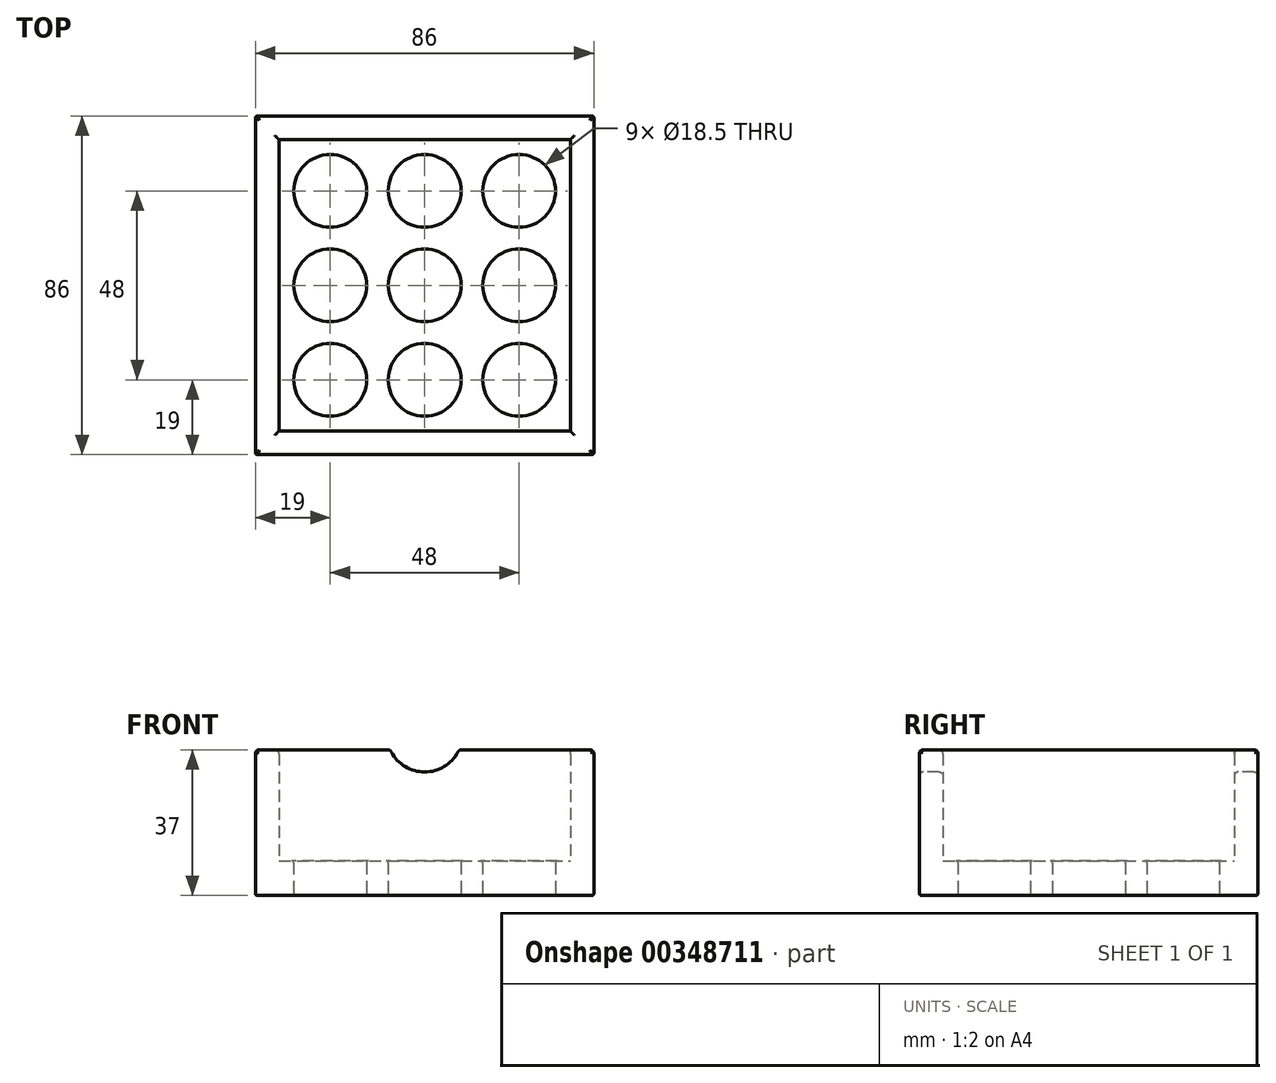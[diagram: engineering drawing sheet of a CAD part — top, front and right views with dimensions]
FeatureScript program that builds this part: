
annotation { "Feature Type Name" : "Feature", "Feature Type Description" : "" }
export const myFeature = defineFeature(function(context is Context, id is Id, definition is map)
    precondition{}
    {
        {
            var Q0;
            Q0=qCreatedBy(makeId("Top.planeOp"),FACE);
            var sketch = newSketch(context, id + "F0", { "sketchPlane" : qUnion([Q0])});
            skLineSegment(sketch, "E0.bottom", {"start": v(0, 0) * mm, "end": v(74, 0) * mm});
            skLineSegment(sketch, "E0.top", {"start": v(0, 74) * mm, "end": v(74, 74) * mm});
            skLineSegment(sketch, "E0.left", {"start": v(0, 0) * mm, "end": v(0, 74) * mm});
            skLineSegment(sketch, "E0.right", {"start": v(74, 0) * mm, "end": v(74, 74) * mm});
            skCircle(sketch, "E1", {"center": v(13, 13) * mm, "radius": 9.25 * mm});
            skCircle(sketch, "E2.0.1.0", {"center": v(13, 37) * mm, "radius": 9.25 * mm});
            skCircle(sketch, "E2.0.2.0", {"center": v(13, 61) * mm, "radius": 9.25 * mm});
            skCircle(sketch, "E2.1.0.0", {"center": v(37, 13) * mm, "radius": 9.25 * mm});
            skCircle(sketch, "E2.1.1.0", {"center": v(37, 37) * mm, "radius": 9.25 * mm});
            skCircle(sketch, "E2.1.2.0", {"center": v(37, 61) * mm, "radius": 9.25 * mm});
            skCircle(sketch, "E2.2.0.0", {"center": v(61, 13) * mm, "radius": 9.25 * mm});
            skCircle(sketch, "E2.2.1.0", {"center": v(61, 37) * mm, "radius": 9.25 * mm});
            skCircle(sketch, "E2.2.2.0", {"center": v(61, 61) * mm, "radius": 9.25 * mm});
            skLineSegment(sketch, "E2.direction1", {"start": v(13, 13) * mm, "end": v(37, 13) * mm, "construction": true});
            skLineSegment(sketch, "E2.direction2", {"start": v(13, 13) * mm, "end": v(13, 37) * mm, "construction": true});
            skLineSegment(sketch, "E3", {"start": v(0, 0) * mm, "end": v(-6, 0) * mm, "construction": true});
            skLineSegment(sketch, "E4", {"start": v(-6, 0) * mm, "end": v(-6, -6) * mm});
            skLineSegment(sketch, "E5.bottom", {"start": v(-6, -6) * mm, "end": v(80, -6) * mm});
            skLineSegment(sketch, "E5.top", {"start": v(-6, 80) * mm, "end": v(80, 80) * mm});
            skLineSegment(sketch, "E5.left", {"start": v(-6, -6) * mm, "end": v(-6, 80) * mm});
            skLineSegment(sketch, "E5.right", {"start": v(80, -6) * mm, "end": v(80, 80) * mm});
            skLineSegment(sketch, "E6", {"start": v(74, 74) * mm, "end": v(80, 74) * mm, "construction": true});
            skLineSegment(sketch, "E7", {"start": v(80, 74) * mm, "end": v(74, 74) * mm, "construction": true});
            skLineSegment(sketch, "E8", {"start": v(74, 74) * mm, "end": v(74, 80) * mm, "construction": true});
            skSolve(sketch);
        }
        {
            var Q0;
            Q0=makeQuery(id+"F0.imprint","IMPRINT",FACE,{"disambiguationData":[TD([[makeQuery(id+"F0.imprint","IMPRINT",EDGE,{"derivedFrom":sQuery(id+"F0.wireOp",EDGE,"E0.bottom")}),-1.0]])]});
            extrude(context, id + "F1", {"entities" : qUnion([Q0]), "depth" : 37 * mm});
        }
        {
            var Q0;
            Q0=makeQuery(id+"F0.imprint","IMPRINT",FACE,{"disambiguationData":[TD([[makeQuery(id+"F0.imprint","IMPRINT",EDGE,{"derivedFrom":sQuery(id+"F0.wireOp",EDGE,"E0.bottom")}),1.0]])]});
            extrude(context, id + "F2", {"entities" : qUnion([Q0]), "operationType" : NewBodyOperationType.ADD, "depth" : 8.8 * mm});
        }
        {
            var Q0;
            Q0=makeQuery(id+"F1.opExtrude","SWEPT_FACE",FACE,{"disambiguationData":[OSD([sQuery(id+"F0.wireOp",EDGE,"E5.bottom")])]});
            var sketch = newSketch(context, id + "F3", { "sketchPlane" : qUnion([Q0])});
            skLineSegment(sketch, "E9", {"start": v(37, 37) * mm, "end": v(37, 41) * mm, "construction": true});
            skPoint(sketch, "E9.endSnap0", {"position": v(37, 37) * mm});
            skCircle(sketch, "E10", {"center": v(37, 41) * mm, "radius": 9.64 * mm});
            skSolve(sketch);
        }
        {
            var Q0;
            Q0 = qSketchRegion(id + "F3", true);
            extrude(context, id + "F4", {"entities" : qUnion([Q0]), "operationType" : NewBodyOperationType.REMOVE, "oppositeDirection" : true, "depth" : 800 * mm});
        }
        {
            var Q0;
            {var subQ0=sQuery(id+"F0.wireOp",EDGE,"E5.bottom");var subQ1=sQuery(id+"F0.wireOp",EDGE,"E0.left");var subQ2=sQuery(id+"F0.wireOp",EDGE,"E0.top");var subQ3=sQuery(id+"F0.wireOp",EDGE,"E0.bottom");var subQ4=sQuery(id+"F0.wireOp",EDGE,"E5.top");var subQ5=sQuery(id+"F0.wireOp",EDGE,"E5.left");Q0=makeQuery(id+"F4.boolean.opBoolean","SPLIT",FACE,{"disambiguationData":[TD([makeQuery(id+"F1.opExtrude","SWEPT_FACE",FACE,{"disambiguationData":[OSD([subQ1])]})])],"derivedFrom":makeQuery(id+"F1.opExtrude","CAP_FACE",FACE,{"disambiguationData":[OSD([subQ3,subQ2,subQ1,sQuery(id+"F0.wireOp",EDGE,"E0.right"),subQ0,subQ4,subQ5,sQuery(id+"F0.wireOp",EDGE,"E5.right")])],"isStart":false})});}
            var Q1;
            {var subQ0=sQuery(id+"F0.wireOp",EDGE,"E5.right");var subQ1=sQuery(id+"F0.wireOp",EDGE,"E5.bottom");Q1=makeQuery(id+"F4.boolean.opBoolean","SPLIT",EDGE,{"disambiguationData":[TD([makeQuery(id+"F1.opExtrude","SWEPT_FACE",FACE,{"disambiguationData":[OSD([subQ0])]})])],"derivedFrom":makeQuery(id+"F1.opExtrude","CAP_EDGE",EDGE,{"disambiguationData":[OSD([subQ1])],"isStart":false})});}
            var Q2;
            {var subQ0=sQuery(id+"F0.wireOp",EDGE,"E5.bottom");var subQ1=sQuery(id+"F0.wireOp",EDGE,"E0.top");var subQ2=sQuery(id+"F0.wireOp",EDGE,"E0.right");var subQ3=sQuery(id+"F0.wireOp",EDGE,"E0.bottom");var subQ4=sQuery(id+"F0.wireOp",EDGE,"E5.top");var subQ5=sQuery(id+"F0.wireOp",EDGE,"E5.right");Q2=makeQuery(id+"F4.boolean.opBoolean","SPLIT",FACE,{"disambiguationData":[TD([makeQuery(id+"F1.opExtrude","SWEPT_FACE",FACE,{"disambiguationData":[OSD([subQ2])]})])],"derivedFrom":makeQuery(id+"F1.opExtrude","CAP_FACE",FACE,{"disambiguationData":[OSD([subQ3,subQ1,sQuery(id+"F0.wireOp",EDGE,"E0.left"),subQ2,subQ0,subQ4,sQuery(id+"F0.wireOp",EDGE,"E5.left"),subQ5])],"isStart":false})});}
            var Q3;
            {var subQ0=sQuery(id+"F0.wireOp",EDGE,"E0.bottom");Q3=makeQuery(id+"F4.boolean.opBoolean","COPY",FACE,{"disambiguationData":[TD([makeQuery(id+"F1.opExtrude","SWEPT_FACE",FACE,{"disambiguationData":[OSD([subQ0])]})])],"derivedFrom":makeQuery(id+"F4.opExtrude","SWEPT_FACE",FACE,{"disambiguationData":[OSD([sQuery(id+"F3.wireOp",EDGE,"E10")])]})});}
            var Q4;
            {var subQ1=sQuery(id+"F0.wireOp",EDGE,"E0.top");Q4=makeQuery(id+"F4.boolean.opBoolean","COPY",FACE,{"disambiguationData":[TD([makeQuery(id+"F1.opExtrude","SWEPT_FACE",FACE,{"disambiguationData":[OSD([subQ1])]})])],"derivedFrom":makeQuery(id+"F4.opExtrude","SWEPT_FACE",FACE,{"disambiguationData":[OSD([sQuery(id+"F3.wireOp",EDGE,"E10")])]})});}
            fillet(context, id + "F5", {"entities" : qUnion([Q0, Q1, Q2, Q3, Q4]), "radius" : 1 * mm, "tangentPropagation" : true, "allowEdgeOverflow" : false});
        }
        {
            var Q0;
            Q0=makeQuery(id+"F1.opExtrude","SWEPT_FACE",FACE,{"disambiguationData":[OSD([sQuery(id+"F0.wireOp",EDGE,"E5.bottom")])]});
            var Q1;
            Q1=makeQuery(id+"F1.opExtrude","SWEPT_FACE",FACE,{"disambiguationData":[OSD([sQuery(id+"F0.wireOp",EDGE,"E5.right")])]});
            var Q2;
            Q2=makeQuery(id+"F1.opExtrude","SWEPT_FACE",FACE,{"disambiguationData":[OSD([sQuery(id+"F0.wireOp",EDGE,"E5.left")])]});
            var Q3;
            Q3=makeQuery(id+"F1.opExtrude","SWEPT_FACE",FACE,{"disambiguationData":[OSD([sQuery(id+"F0.wireOp",EDGE,"E5.top")])]});
            fillet(context, id + "F6", {"entities" : qUnion([Q0, Q1, Q2, Q3]), "radius" : 0.5 * mm, "tangentPropagation" : true, "allowEdgeOverflow" : false});
        }
        {
            var Q0;
            Q0=makeQuery(id+"F2.opExtrude","SWEPT_FACE",FACE,{"disambiguationData":[OSD([sQuery(id+"F0.wireOp",EDGE,"E2.2.0.0")])]});
            var Q1;
            Q1=makeQuery(id+"F2.opExtrude","SWEPT_FACE",FACE,{"disambiguationData":[OSD([sQuery(id+"F0.wireOp",EDGE,"E2.2.1.0")])]});
            var Q2;
            Q2=makeQuery(id+"F2.opExtrude","SWEPT_FACE",FACE,{"disambiguationData":[OSD([sQuery(id+"F0.wireOp",EDGE,"E2.2.2.0")])]});
            var Q3;
            Q3=makeQuery(id+"F2.opExtrude","SWEPT_FACE",FACE,{"disambiguationData":[OSD([sQuery(id+"F0.wireOp",EDGE,"E2.1.2.0")])]});
            var Q4;
            Q4=makeQuery(id+"F2.opExtrude","SWEPT_FACE",FACE,{"disambiguationData":[OSD([sQuery(id+"F0.wireOp",EDGE,"E2.1.1.0")])]});
            var Q5;
            Q5=makeQuery(id+"F2.opExtrude","SWEPT_FACE",FACE,{"disambiguationData":[OSD([sQuery(id+"F0.wireOp",EDGE,"E2.1.0.0")])]});
            var Q6;
            Q6=makeQuery(id+"F2.opExtrude","SWEPT_FACE",FACE,{"disambiguationData":[OSD([sQuery(id+"F0.wireOp",EDGE,"E1")])]});
            var Q7;
            Q7=makeQuery(id+"F2.opExtrude","SWEPT_FACE",FACE,{"disambiguationData":[OSD([sQuery(id+"F0.wireOp",EDGE,"E2.0.1.0")])]});
            var Q8;
            Q8=makeQuery(id+"F2.opExtrude","SWEPT_FACE",FACE,{"disambiguationData":[OSD([sQuery(id+"F0.wireOp",EDGE,"E2.0.2.0")])]});
            fillet(context, id + "F7", {"entities" : qUnion([Q0, Q1, Q2, Q3, Q4, Q5, Q6, Q7, Q8]), "radius" : 0.5 * mm, "tangentPropagation" : true, "allowEdgeOverflow" : false});
        }
    });
